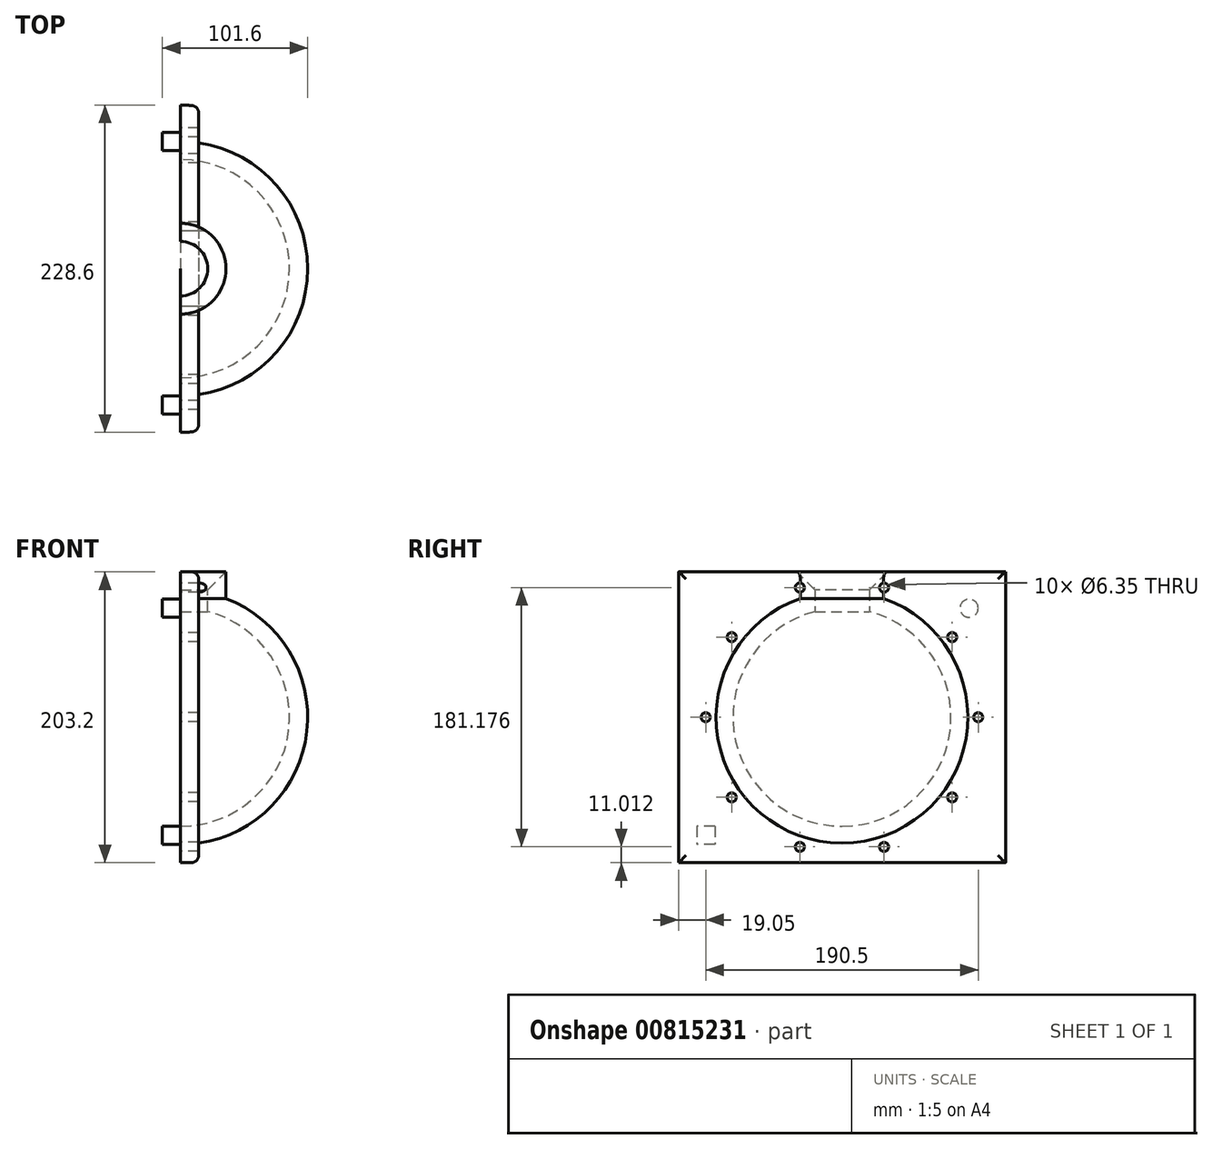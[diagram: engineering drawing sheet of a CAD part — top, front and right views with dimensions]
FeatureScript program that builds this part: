
annotation { "Feature Type Name" : "Feature", "Feature Type Description" : "" }
export const myFeature = defineFeature(function(context is Context, id is Id, definition is map)
    precondition{}
    {
        {
            var Q0;
            Q0=qCreatedBy(makeId("Right.planeOp"),FACE);
            var sketch = newSketch(context, id + "F0", { "sketchPlane" : qUnion([Q0])});
            skCircle(sketch, "E0", {"center": v(0, 0) * mm, "radius": 76.2 * mm});
            skLineSegment(sketch, "E1", {"start": v(0, -76.2) * mm, "end": v(0, -101.6) * mm});
            skLineSegment(sketch, "E2", {"start": v(0, -101.6) * mm, "end": v(114.3, -101.6) * mm});
            skLineSegment(sketch, "E3", {"start": v(114.3, -101.6) * mm, "end": v(114.3, 101.6) * mm});
            skLineSegment(sketch, "E4", {"start": v(114.3, 101.6) * mm, "end": v(19.05, 101.6) * mm});
            skLineSegment(sketch, "E5", {"start": v(19.05, 101.6) * mm, "end": v(19.05, 73.78) * mm});
            skSolve(sketch);
        }
        {
            var Q0;
            {var subQ0=sQuery(id+"F0.wireOp",EDGE,"E1");Q0=makeQuery(id+"F0.imprint","IMPRINT",FACE,{"disambiguationData":[TD([[makeQuery(id+"F0.imprint","IMPRINT",EDGE,{"derivedFrom":subQ0}),1.0]])]});}
            var Q1;
            Q1=sQuery(id+"F0.wireOp",EDGE,"E1");
            revolve(context, id + "F1", {"surfaceOperationType" : NewSurfaceOperationType.NEW, "entities" : qUnion([Q0]), "axis" : qUnion([Q1]), "revolveType" : RevolveType.ONE_DIRECTION, "angle" : 180 * degree});
        }
        {
            var Q0;
            Q0=makeQuery(id+"F1.opRevolve","CAP_FACE",FACE,{"disambiguationData":[OSD([sQuery(id+"F0.wireOp",EDGE,"E0"),sQuery(id+"F0.wireOp",EDGE,"E1"),sQuery(id+"F0.wireOp",EDGE,"E2"),sQuery(id+"F0.wireOp",EDGE,"E3"),sQuery(id+"F0.wireOp",EDGE,"E4"),sQuery(id+"F0.wireOp",EDGE,"E5")])],"isStart":false});
            var sketch = newSketch(context, id + "F2", { "sketchPlane" : qUnion([Q0])});
            skCircle(sketch, "E6", {"center": v(-88.9, 76.2) * mm, "radius": 6.35 * mm});
            skLineSegment(sketch, "E7.bottom", {"start": v(88.9, -76.2) * mm, "end": v(101.6, -76.2) * mm});
            skLineSegment(sketch, "E7.top", {"start": v(88.9, -88.9) * mm, "end": v(101.6, -88.9) * mm});
            skLineSegment(sketch, "E7.left", {"start": v(88.9, -76.2) * mm, "end": v(88.9, -88.9) * mm});
            skLineSegment(sketch, "E7.right", {"start": v(101.6, -76.2) * mm, "end": v(101.6, -88.9) * mm});
            skCircle(sketch, "E8.MirrorC", {"center": v(88.9, 76.2) * mm, "radius": 6.35 * mm});
            skLineSegment(sketch, "E9.MirrorCS", {"start": v(-88.9, -76.2) * mm, "end": v(-101.6, -76.2) * mm});
            skLineSegment(sketch, "E10.MirrorCS", {"start": v(-101.6, -76.2) * mm, "end": v(-101.6, -88.9) * mm});
            skLineSegment(sketch, "E11.MirrorCS", {"start": v(-88.9, -88.9) * mm, "end": v(-101.6, -88.9) * mm});
            skLineSegment(sketch, "E12.MirrorCS", {"start": v(-88.9, -76.2) * mm, "end": v(-88.9, -88.9) * mm});
            skSolve(sketch);
        }
        {
            var Q0;
            Q0=makeQuery(id+"F2.imprint","IMPRINT",FACE,{"disambiguationData":[TD([[makeQuery(id+"F2.imprint","IMPRINT",EDGE,{"derivedFrom":sQuery(id+"F2.wireOp",EDGE,"E6")}),1.0]])]});
            var Q1;
            Q1=makeQuery(id+"F2.imprint","IMPRINT",FACE,{"disambiguationData":[TD([[makeQuery(id+"F2.imprint","IMPRINT",EDGE,{"derivedFrom":sQuery(id+"F2.wireOp",EDGE,"E7.bottom")}),-1.0]])]});
            extrude(context, id + "F3", {"entities" : qUnion([Q0, Q1]), "operationType" : NewBodyOperationType.ADD, "depth" : 12.7 * mm, "offsetDistance" : 25.4 * mm});
        }
        {
            var Q0;
            Q0=makeQuery(id+"F1.opRevolve","SWEPT_FACE",FACE,{"disambiguationData":[OSD([sQuery(id+"F0.wireOp",EDGE,"E3")])]});
            var Q1;
            Q1=makeQuery(id+"F1.opRevolve","SWEPT_FACE",FACE,{"disambiguationData":[OSD([sQuery(id+"F0.wireOp",EDGE,"E2")])]});
            var Q2;
            Q2=makeQuery(id+"F1.opRevolve","SWEPT_FACE",FACE,{"disambiguationData":[OSD([sQuery(id+"F0.wireOp",EDGE,"E4")])]});
            shell(context, id + "F4", {"entities" : qUnion([Q0, Q1, Q2]), "thickness" : 12.7 * mm});
        }
        {
            var Q0;
            {var subQ0=sQuery(id+"F0.wireOp",EDGE,"E3");Q0=makeQuery(id+"F4.opShell","OFFSET_EDGE",EDGE,{"disambiguationData":[OSD([subQ0]),TDD([makeQuery(id+"F1.opRevolve","CAP_EDGE",EDGE,{"disambiguationData":[OSD([subQ0])],"isStart":false})])]});}
            var Q1;
            Q1=makeQuery(id+"F4.opShell","OFFSET_EDGE",EDGE,{"disambiguationData":[OSD([sQuery(id+"F0.wireOp",EDGE,"E2")])]});
            var Q2;
            {var subQ0=sQuery(id+"F0.wireOp",EDGE,"E3");Q2=makeQuery(id+"F4.opShell","OFFSET_EDGE",EDGE,{"disambiguationData":[OSD([subQ0]),TDD([makeQuery(id+"F1.opRevolve","CAP_EDGE",EDGE,{"disambiguationData":[OSD([subQ0])],"isStart":true})])]});}
            var Q3;
            {var subQ0=sQuery(id+"F0.wireOp",EDGE,"E4");Q3=makeQuery(id+"F4.opShell","OFFSET_EDGE",EDGE,{"disambiguationData":[OSD([subQ0]),TDD([makeQuery(id+"F1.opRevolve","CAP_EDGE",EDGE,{"disambiguationData":[OSD([subQ0])],"isStart":true})])]});}
            var Q4;
            {var subQ0=sQuery(id+"F0.wireOp",EDGE,"E4");Q4=makeQuery(id+"F4.opShell","OFFSET_EDGE",EDGE,{"disambiguationData":[OSD([subQ0]),TDD([makeQuery(id+"F1.opRevolve","CAP_EDGE",EDGE,{"disambiguationData":[OSD([subQ0])],"isStart":false})])]});}
            fillet(context, id + "F5", {"entities" : qUnion([Q0, Q1, Q2, Q3, Q4]), "radius" : 5.08 * mm, "tangentPropagation" : true, "allowEdgeOverflow" : false});
        }
        {
            var Q0;
            Q0=makeQuery(id+"F1.opRevolve","SWEPT_EDGE",EDGE,{"disambiguationData":[OSD([sQuery(id+"F0.wireOp",EDGE,"E4"),sQuery(id+"F0.wireOp",EDGE,"E5")])]});
            chamfer(context, id + "F6", {"entities" : qUnion([Q0]), "width" : 12.7 * mm, "tangentPropagation" : true});
        }
        {
            var Q0;
            Q0=makeQuery(id+"F1.opRevolve","CAP_FACE",FACE,{"disambiguationData":[OSD([sQuery(id+"F0.wireOp",EDGE,"E0"),sQuery(id+"F0.wireOp",EDGE,"E1"),sQuery(id+"F0.wireOp",EDGE,"E2"),sQuery(id+"F0.wireOp",EDGE,"E3"),sQuery(id+"F0.wireOp",EDGE,"E4"),sQuery(id+"F0.wireOp",EDGE,"E5")])],"isStart":false});
            var sketch = newSketch(context, id + "F7", { "sketchPlane" : qUnion([Q0])});
            skCircle(sketch, "E13", {"center": v(-95.25, 0) * mm, "radius": 3.18 * mm});
            skCircle(sketch, "E14.1.0", {"center": v(-77.06, -55.99) * mm, "radius": 3.18 * mm});
            skCircle(sketch, "E14.2.0", {"center": v(-29.43, -90.59) * mm, "radius": 3.18 * mm});
            skCircle(sketch, "E14.3.0", {"center": v(29.43, -90.59) * mm, "radius": 3.18 * mm});
            skCircle(sketch, "E14.4.0", {"center": v(77.06, -55.99) * mm, "radius": 3.18 * mm});
            skCircle(sketch, "E14.5.0", {"center": v(95.25, 0) * mm, "radius": 3.18 * mm});
            skCircle(sketch, "E14.6.0", {"center": v(77.06, 55.99) * mm, "radius": 3.18 * mm});
            skCircle(sketch, "E14.7.0", {"center": v(29.43, 90.59) * mm, "radius": 3.18 * mm});
            skCircle(sketch, "E14.8.0", {"center": v(-29.43, 90.59) * mm, "radius": 3.18 * mm});
            skCircle(sketch, "E14.9.0", {"center": v(-77.06, 55.99) * mm, "radius": 3.18 * mm});
            skPoint(sketch, "E14.center", {"position": v(0, 0) * mm});
            skSolve(sketch);
        }
        {
            var Q0;
            Q0=qSketchRegion(id+"F7",true);
            extrude(context, id + "F8", {"entities" : qUnion([Q0]), "operationType" : NewBodyOperationType.REMOVE, "endBound" : BoundingType.THROUGH_ALL, "oppositeDirection" : true, "depth" : 25.4 * mm, "offsetDistance" : 25.4 * mm});
        }
    });
